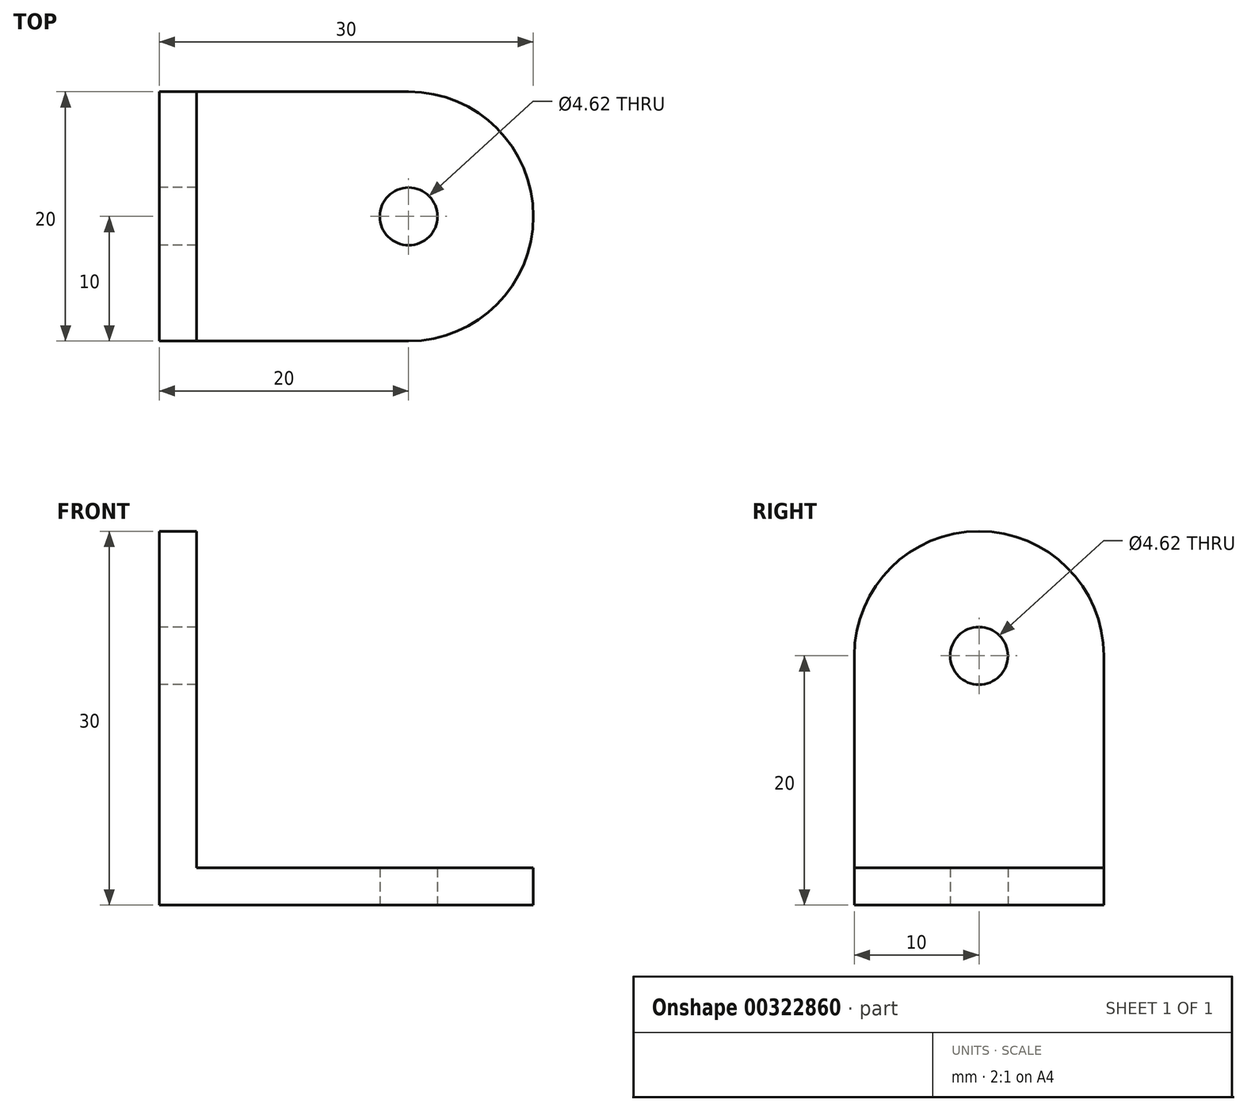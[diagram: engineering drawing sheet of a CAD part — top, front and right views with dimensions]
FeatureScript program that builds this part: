
annotation { "Feature Type Name" : "Feature", "Feature Type Description" : "" }
export const myFeature = defineFeature(function(context is Context, id is Id, definition is map)
    precondition{}
    {
        {
            var Q0;
            Q0=qCreatedBy(makeId("Top.planeOp"),FACE);
            var sketch = newSketch(context, id + "F0", { "sketchPlane" : qUnion([Q0])});
            skLineSegment(sketch, "E0.bottom", {"start": v(10, -10) * mm, "end": v(-10, -10) * mm});
            skLineSegment(sketch, "E0.top", {"start": v(10, 10) * mm, "end": v(-10, 10) * mm});
            skLineSegment(sketch, "E0.left", {"start": v(10, -10) * mm, "end": v(10, 10) * mm});
            skLineSegment(sketch, "E0.right", {"start": v(-10, -10) * mm, "end": v(-10, 10) * mm});
            skPoint(sketch, "E0.middle", {"position": v(0, 0) * mm});
            skCircle(sketch, "E1", {"center": v(10, 0) * mm, "radius": 10 * mm});
            skCircle(sketch, "E2", {"center": v(10, 0) * mm, "radius": 2.31 * mm});
            skSolve(sketch);
        }
        {
            var Q0;
            Q0 = qSketchRegion(id + "F0", true);
            extrude(context, id + "F1", {"entities" : qUnion([Q0]), "depth" : 3 * mm});
        }
        {
            var Q0;
            Q0=makeQuery(id+"F1.opExtrude","SWEPT_FACE",FACE,{"disambiguationData":[OSD([sQuery(id+"F0.wireOp",EDGE,"E0.right")])]});
            var sketch = newSketch(context, id + "F2", { "sketchPlane" : qUnion([Q0])});
            skLineSegment(sketch, "E3.bottom", {"start": v(-10, 0) * mm, "end": v(10, 0) * mm});
            skLineSegment(sketch, "E3.top", {"start": v(-10, 20) * mm, "end": v(10, 20) * mm});
            skLineSegment(sketch, "E3.left", {"start": v(-10, 0) * mm, "end": v(-10, 20) * mm});
            skLineSegment(sketch, "E3.right", {"start": v(10, 0) * mm, "end": v(10, 20) * mm});
            skCircle(sketch, "E4", {"center": v(0, 20) * mm, "radius": 10 * mm});
            skCircle(sketch, "E5", {"center": v(0, 20) * mm, "radius": 2.31 * mm});
            skSolve(sketch);
        }
        {
            var Q0;
            Q0 = qSketchRegion(id + "F2", true);
            extrude(context, id + "F3", {"entities" : qUnion([Q0]), "operationType" : NewBodyOperationType.ADD, "depth" : -3 * mm});
        }
    });
